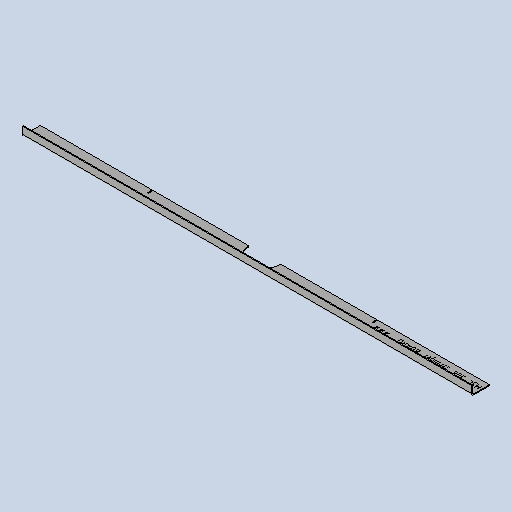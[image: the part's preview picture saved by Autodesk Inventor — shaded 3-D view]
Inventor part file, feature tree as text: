
AUTODESK INVENTOR PART (.ipt)
format: ipt  version: 2025 (Build 290162010, 162A)  size: 331,264 bytes
history: native  units: mm
features: other x5, sheet_metal_op x4, sketch x4, extrude x1
ambient origin geometry x8: Origin, YZ Plane, XZ Plane, XY Plane, X Axis, Y Axis, Z Axis, Center Point
bodies: Solid1 (feature_tree)
feature tree (14):
  sheet_metal_op  "Face1"
  sheet_metal_op  "Flange1"
  extrude  "Extrusion1"  Depth=39.0mm
  other  "Mark2"
  other  "A-Side Definition"
  sketch  "Sketch1"  dims[d0=980.0mm d1=39.0mm]
  other  "Plate1"
  sketch  "Sketch2"  dims[d2=2.0mm]
  other  "Plate2"
  sheet_metal_op  "Bend1"
  sheet_metal_op  "Corner1"
  sketch  "Sketch5"  dims[d3=2.0mm]
  sketch  "Sketch9"  dims[d4=1.0mm d5=4.0mm d6=2.75mm d7=20.0mm d8=90.0deg d9=2.75mm d10=8.0mm d11=2.0mm d12=2.75mm d15=0.0mm d16=0.0mm d40=200.0mm d41=12.0mm d45=70.0mm d48=2.1mm d49=490.0mm d51=29.0mm d52=10.0mm]
  other  "Definition1"
